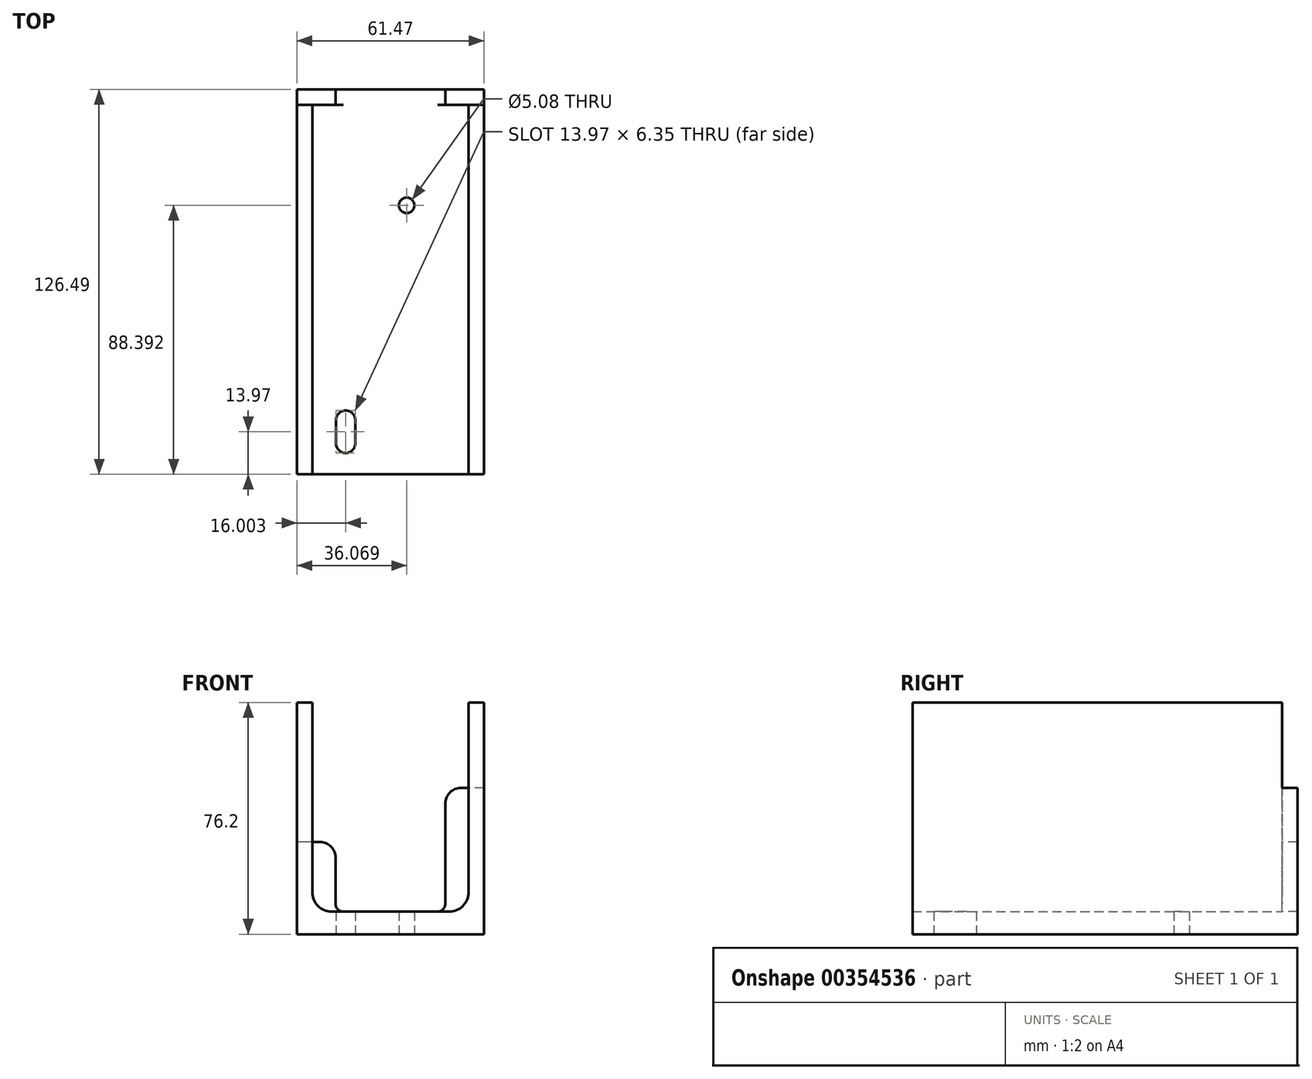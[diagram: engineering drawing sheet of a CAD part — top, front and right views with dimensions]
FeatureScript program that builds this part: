
annotation { "Feature Type Name" : "Feature", "Feature Type Description" : "" }
export const myFeature = defineFeature(function(context is Context, id is Id, definition is map)
    precondition{}
    {
        {
            var Q0;
            Q0=qCreatedBy(makeId("Front.planeOp"),FACE);
            var sketch = newSketch(context, id + "F0", { "sketchPlane" : qUnion([Q0])});
            skSolve(sketch);
        }
        {
            var Q0;
            Q0=qCreatedBy(makeId("Front.planeOp"),FACE);
            var sketch = newSketch(context, id + "F1", { "sketchPlane" : qUnion([Q0])});
            skLineSegment(sketch, "E0", {"start": v(-64.72, 100.4) * mm, "end": v(-64.72, 37.96) * mm});
            skLineSegment(sketch, "E1", {"start": v(-58.37, 31.61) * mm, "end": v(-19.76, 31.61) * mm});
            skLineSegment(sketch, "E2", {"start": v(-13.41, 37.96) * mm, "end": v(-13.41, 100.4) * mm});
            skLineSegment(sketch, "E3", {"start": v(-13.41, 100.4) * mm, "end": v(-8.33, 100.4) * mm});
            skLineSegment(sketch, "E4", {"start": v(-8.33, 100.4) * mm, "end": v(-8.33, 24.2) * mm});
            skLineSegment(sketch, "E5", {"start": v(-8.33, 24.2) * mm, "end": v(-69.8, 24.2) * mm});
            skLineSegment(sketch, "E6", {"start": v(-69.8, 24.2) * mm, "end": v(-69.8, 100.4) * mm});
            skLineSegment(sketch, "E7", {"start": v(-69.8, 100.4) * mm, "end": v(-64.72, 100.4) * mm});
            skPoint(sketch, "E8.visualSharp", {"position": v(-64.72, 31.61) * mm});
            skArc(sketch, "E8.filletArc", {"start": v(-64.72, 37.96) * mm, "mid": v(-62.86, 33.47) * mm, "end": v(-58.37, 31.61) * mm});
            skPoint(sketch, "E9.visualSharp", {"position": v(-13.41, 31.61) * mm});
            skArc(sketch, "E9.filletArc", {"start": v(-19.76, 31.61) * mm, "mid": v(-15.27, 33.47) * mm, "end": v(-13.41, 37.96) * mm});
            skSolve(sketch);
        }
        {
            var Q0;
            Q0=makeQuery(id+"F1.imprint","IMPRINT",FACE,{"disambiguationData":[TD([[makeQuery(id+"F1.imprint","IMPRINT",EDGE,{"derivedFrom":sQuery(id+"F1.wireOp",EDGE,"E0")}),-1.0]])]});
            var Q1;
            Q1 = qSketchRegion(id + "F0", true);
            extrude(context, id + "F2", {"entities" : qUnion([Q0, Q1]), "depth" : 38.1 * mm});
        }
        {
            var Q0;
            Q0=makeQuery(id+"F2.opExtrude","CAP_FACE",FACE,{"disambiguationData":[OSD([sQuery(id+"F1.wireOp",EDGE,"E0"),sQuery(id+"F1.wireOp",EDGE,"E1"),sQuery(id+"F1.wireOp",EDGE,"E2"),sQuery(id+"F1.wireOp",EDGE,"E3"),sQuery(id+"F1.wireOp",EDGE,"E4"),sQuery(id+"F1.wireOp",EDGE,"E5"),sQuery(id+"F1.wireOp",EDGE,"E6"),sQuery(id+"F1.wireOp",EDGE,"E7"),sQuery(id+"F1.wireOp",EDGE,"E8.filletArc"),sQuery(id+"F1.wireOp",EDGE,"E9.filletArc")])],"isStart":true});
            extrude(context, id + "F3", {"entities" : qUnion([Q0]), "operationType" : NewBodyOperationType.ADD, "depth" : 83.31 * mm});
        }
        {
            var Q0;
            {var subQ0=sQuery(id+"F1.wireOp",EDGE,"E5");Q0=makeQuery(id+"F3.boolean.opBoolean","MERGE",FACE,{"derivedFrom":[makeQuery(id+"F2.opExtrude","SWEPT_FACE",FACE,{"disambiguationData":[OSD([subQ0])]}),makeQuery(id+"F3.opExtrude","SWEPT_FACE",FACE,{"disambiguationData":[OSD([subQ0])]})]});}
            var sketch = newSketch(context, id + "F4", { "sketchPlane" : qUnion([Q0])});
            skArc(sketch, "E10", {"start": v(-50.62, 27.94) * mm, "mid": v(-53.8, 31.12) * mm, "end": v(-56.97, 27.94) * mm});
            skArc(sketch, "E11", {"start": v(-56.97, 20.32) * mm, "mid": v(-53.8, 17.14) * mm, "end": v(-50.62, 20.32) * mm});
            skLineSegment(sketch, "E12", {"start": v(-56.97, 27.94) * mm, "end": v(-56.97, 20.32) * mm});
            skLineSegment(sketch, "E13", {"start": v(-50.62, 27.94) * mm, "end": v(-50.62, 20.32) * mm});
            skSolve(sketch);
        }
        {
            var Q0;
            Q0 = qSketchRegion(id + "F4", true);
            extrude(context, id + "F5", {"entities" : qUnion([Q0]), "operationType" : NewBodyOperationType.REMOVE, "oppositeDirection" : true, "depth" : 25.4 * mm});
        }
        {
            var Q0;
            Q0=makeQuery(id+"F3.opExtrude","CAP_FACE",FACE,{"disambiguationData":[OSD([sQuery(id+"F1.wireOp",EDGE,"E0"),sQuery(id+"F1.wireOp",EDGE,"E1"),sQuery(id+"F1.wireOp",EDGE,"E2"),sQuery(id+"F1.wireOp",EDGE,"E3"),sQuery(id+"F1.wireOp",EDGE,"E4"),sQuery(id+"F1.wireOp",EDGE,"E5"),sQuery(id+"F1.wireOp",EDGE,"E6"),sQuery(id+"F1.wireOp",EDGE,"E7"),sQuery(id+"F1.wireOp",EDGE,"E8.filletArc"),sQuery(id+"F1.wireOp",EDGE,"E9.filletArc")])],"isStart":false});
            var sketch = newSketch(context, id + "F6", { "sketchPlane" : qUnion([Q0])});
            skLineSegment(sketch, "E14", {"start": v(8.33, 72.25) * mm, "end": v(21.03, 72.25) * mm});
            skLineSegment(sketch, "E15", {"start": v(21.03, 72.25) * mm, "end": v(21.03, 34.15) * mm});
            skLineSegment(sketch, "E16", {"start": v(23.57, 31.61) * mm, "end": v(54.56, 31.61) * mm});
            skLineSegment(sketch, "E17", {"start": v(57.1, 34.15) * mm, "end": v(57.1, 54.47) * mm});
            skLineSegment(sketch, "E18", {"start": v(57.1, 54.47) * mm, "end": v(69.8, 54.47) * mm});
            skPoint(sketch, "E19.visualSharp", {"position": v(21.03, 31.61) * mm});
            skArc(sketch, "E19.filletArc", {"start": v(21.03, 34.15) * mm, "mid": v(21.78, 32.36) * mm, "end": v(23.57, 31.61) * mm});
            skPoint(sketch, "E20.visualSharp", {"position": v(57.1, 31.61) * mm});
            skArc(sketch, "E20.filletArc", {"start": v(54.56, 31.61) * mm, "mid": v(56.36, 32.36) * mm, "end": v(57.1, 34.15) * mm});
            skLineSegment(sketch, "E21", {"start": v(8.33, 72.25) * mm, "end": v(8.33, 24.2) * mm});
            skLineSegment(sketch, "E22", {"start": v(8.33, 24.2) * mm, "end": v(69.8, 24.2) * mm});
            skLineSegment(sketch, "E23", {"start": v(69.8, 24.2) * mm, "end": v(69.8, 54.47) * mm});
            skSolve(sketch);
        }
        {
            var Q0;
            Q0 = qSketchRegion(id + "F6", true);
            extrude(context, id + "F7", {"entities" : qUnion([Q0]), "operationType" : NewBodyOperationType.ADD, "depth" : 5.08 * mm});
        }
        {
            var Q0;
            {var subQ0=sQuery(id+"F1.wireOp",EDGE,"E5");Q0=makeQuery(id+"F7.boolean.opBoolean","MERGE",FACE,{"derivedFrom":[makeQuery(id+"F3.boolean.opBoolean","MERGE",FACE,{"derivedFrom":[makeQuery(id+"F2.opExtrude","SWEPT_FACE",FACE,{"disambiguationData":[OSD([subQ0])]}),makeQuery(id+"F3.opExtrude","SWEPT_FACE",FACE,{"disambiguationData":[OSD([subQ0])]})]}),makeQuery(id+"F7.opExtrude","SWEPT_FACE",FACE,{"disambiguationData":[OSD([sQuery(id+"F6.wireOp",EDGE,"E22")])]})]});}
            var sketch = newSketch(context, id + "F8", { "sketchPlane" : qUnion([Q0])});
            skPoint(sketch, "E24", {"position": v(-33.73, -50.3) * mm});
            skSolve(sketch);
        }
        {
            var Q0;
            Q0=sQuery(id+"F8.wireOp",VERTEX,"E24");
            var Q1;
            Q1=makeQuery(id+"F2.opExtrude","SWEPT_BODY",BODY,{"disambiguationData":[OSD([sQuery(id+"F1.wireOp",EDGE,"E0"),sQuery(id+"F1.wireOp",EDGE,"E1"),sQuery(id+"F1.wireOp",EDGE,"E2"),sQuery(id+"F1.wireOp",EDGE,"E3"),sQuery(id+"F1.wireOp",EDGE,"E4"),sQuery(id+"F1.wireOp",EDGE,"E5"),sQuery(id+"F1.wireOp",EDGE,"E6"),sQuery(id+"F1.wireOp",EDGE,"E7"),sQuery(id+"F1.wireOp",EDGE,"E8.filletArc"),sQuery(id+"F1.wireOp",EDGE,"E9.filletArc")])]});
            hole(context, id + "F9", {"style" : HoleStyle.SIMPLE, "endStyle" : HoleEndStyle.THROUGH, "holeDiameter" : 5.08 * mm, "isTappedThrough" : true, "tappedDepth" : 12.7 * mm, "tapClearance" : 3, "locations" : qUnion([Q0]), "scope" : qUnion([Q1])});
        }
        {
            var Q0;
            Q0=makeQuery(id+"F7.opExtrude","SWEPT_EDGE",EDGE,{"disambiguationData":[OSD([sQuery(id+"F6.wireOp",EDGE,"E17"),sQuery(id+"F6.wireOp",EDGE,"E18")])]});
            var Q1;
            Q1=makeQuery(id+"F7.opExtrude","SWEPT_EDGE",EDGE,{"disambiguationData":[OSD([sQuery(id+"F6.wireOp",EDGE,"E14"),sQuery(id+"F6.wireOp",EDGE,"E15")])]});
            fillet(context, id + "F10", {"entities" : qUnion([Q0, Q1]), "radius" : 5.08 * mm, "tangentPropagation" : true, "allowEdgeOverflow" : false});
        }
    });
